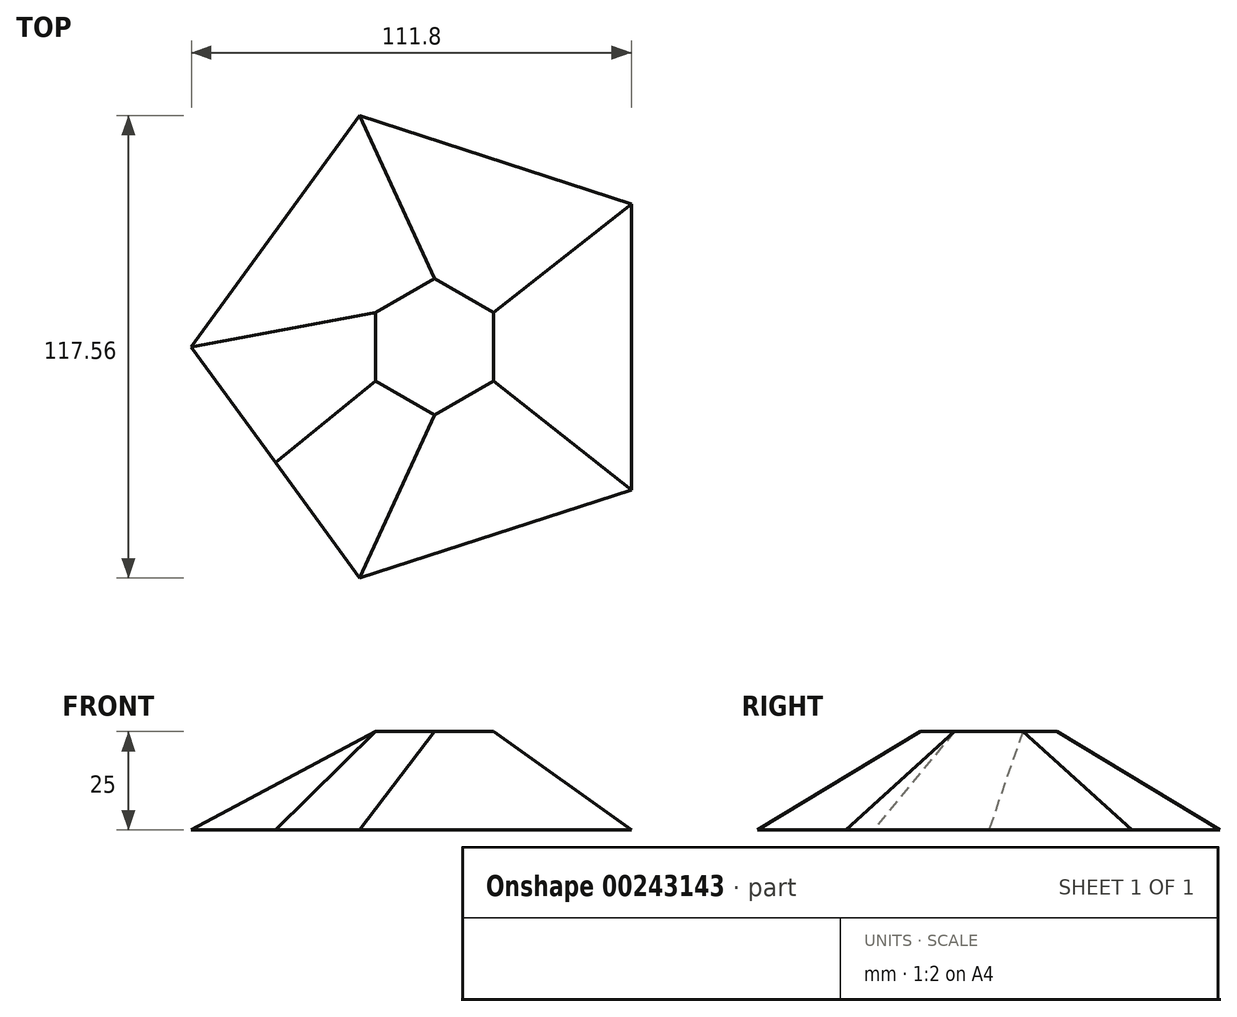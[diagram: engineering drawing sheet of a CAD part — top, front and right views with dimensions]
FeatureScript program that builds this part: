
annotation { "Feature Type Name" : "Feature", "Feature Type Description" : "" }
export const myFeature = defineFeature(function(context is Context, id is Id, definition is map)
    precondition{}
    {
        {
            var Q0;
            Q0=qCreatedBy(makeId("Top.planeOp"),FACE);
            var sketch = newSketch(context, id + "F0", { "sketchPlane" : qUnion([Q0])});
            skCircle(sketch, "E0.cCircle", {"center": v(0, 0) * mm, "radius": 50 * mm, "construction": true});
            skLineSegment(sketch, "E0.0", {"start": v(50, 36.33) * mm, "end": v(50, -36.33) * mm});
            skLineSegment(sketch, "E0.1", {"start": v(50, -36.33) * mm, "end": v(-19.1, -58.78) * mm});
            skLineSegment(sketch, "E0.2", {"start": v(-19.1, -58.78) * mm, "end": v(-61.8, 0) * mm});
            skLineSegment(sketch, "E0.3", {"start": v(-61.8, 0) * mm, "end": v(-19.1, 58.78) * mm});
            skLineSegment(sketch, "E0.4", {"start": v(-19.1, 58.78) * mm, "end": v(50, 36.33) * mm});
            skPoint(sketch, "E0.0.midPoint", {"position": v(50, 0) * mm});
            skSolve(sketch);
        }
        {
            var Q0;
            Q0=qCreatedBy(makeId("Top.planeOp"),FACE);
            cPlane(context, id + "F1", {"entities" : qUnion([Q0]), "cplaneType" : CPlaneType.OFFSET, "offset" : 25 * mm, "width" : 150 * mm, "height" : 150 * mm});
        }
        {
            var Q0;
            Q0=qCreatedBy(id+"F1.planeOp",FACE);
            var sketch = newSketch(context, id + "F2", { "sketchPlane" : qUnion([Q0])});
            skCircle(sketch, "E1.cCircle", {"center": v(0, 0) * mm, "radius": 15 * mm, "construction": true});
            skLineSegment(sketch, "E1.0", {"start": v(15, 8.66) * mm, "end": v(15, -8.66) * mm});
            skLineSegment(sketch, "E1.1", {"start": v(15, -8.66) * mm, "end": v(0, -17.32) * mm});
            skLineSegment(sketch, "E1.2", {"start": v(0, -17.32) * mm, "end": v(-15, -8.66) * mm});
            skLineSegment(sketch, "E1.3", {"start": v(-15, -8.66) * mm, "end": v(-15, 8.66) * mm});
            skLineSegment(sketch, "E1.4", {"start": v(-15, 8.66) * mm, "end": v(0, 17.32) * mm});
            skLineSegment(sketch, "E1.5", {"start": v(0, 17.32) * mm, "end": v(15, 8.66) * mm});
            skPoint(sketch, "E1.0.midPoint", {"position": v(15, 0) * mm});
            skSolve(sketch);
        }
        {
            var Q0;
            Q0=makeQuery(id+"F2.imprint","IMPRINT",FACE,{"disambiguationData":[TD([[makeQuery(id+"F2.imprint","IMPRINT",EDGE,{"derivedFrom":sQuery(id+"F2.wireOp",EDGE,"E1.0")}),-1.0]])]});
            var Q1;
            Q1=makeQuery(id+"F0.imprint","IMPRINT",FACE,{"disambiguationData":[TD([[makeQuery(id+"F0.imprint","IMPRINT",EDGE,{"derivedFrom":sQuery(id+"F0.wireOp",EDGE,"E0.0")}),-1.0]])]});
            loft(context, id + "F3", {"sheetProfilesArray" : [{ "sheetProfileEntities" : qUnion([Q0]) }, { "sheetProfileEntities" : qUnion([Q1]) }]});
        }
    });
